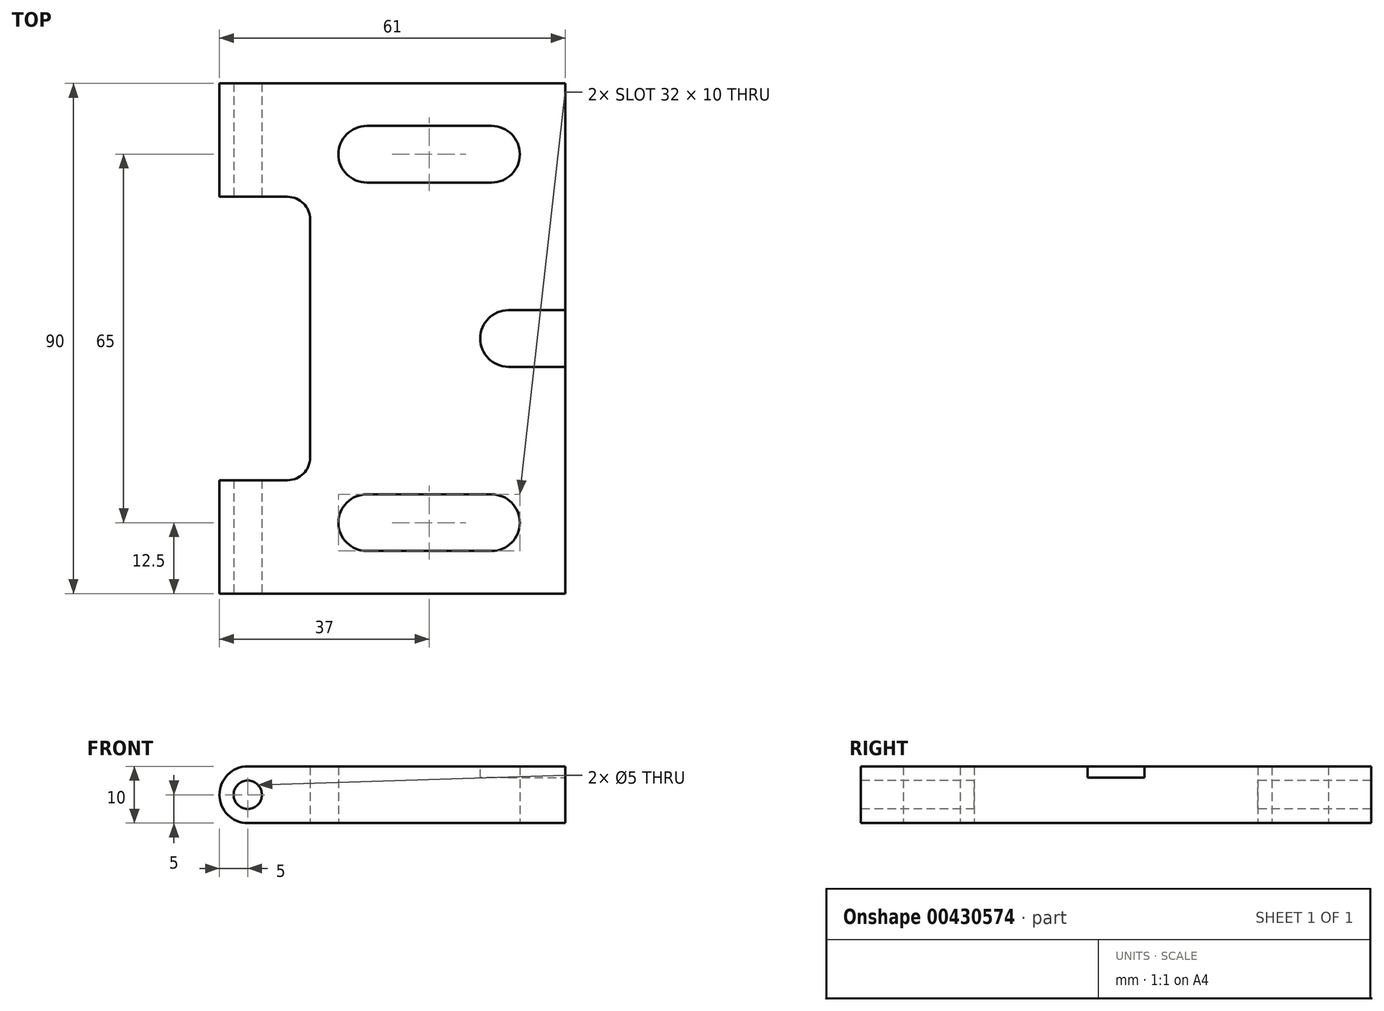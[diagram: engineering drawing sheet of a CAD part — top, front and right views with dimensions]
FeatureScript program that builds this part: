
annotation { "Feature Type Name" : "Feature", "Feature Type Description" : "" }
export const myFeature = defineFeature(function(context is Context, id is Id, definition is map)
    precondition{}
    {
        {
            var Q0;
            Q0=qCreatedBy(makeId("Top.planeOp"),FACE);
            var sketch = newSketch(context, id + "F0", { "sketchPlane" : qUnion([Q0])});
            skLineSegment(sketch, "E0.bottom", {"start": v(56, -45) * mm, "end": v(13, -45) * mm});
            skLineSegment(sketch, "E0.top", {"start": v(56, 45) * mm, "end": v(13, 45) * mm});
            skPoint(sketch, "E0.middle", {"position": v(0, 0) * mm});
            skLineSegment(sketch, "E1.bottom", {"start": v(11, -25) * mm, "end": v(-5, -25) * mm});
            skLineSegment(sketch, "E1.top", {"start": v(11, 25) * mm, "end": v(-5, 25) * mm});
            skPoint(sketch, "E1.middle", {"position": v(13, 0) * mm});
            skLineSegment(sketch, "E2", {"start": v(56, 45) * mm, "end": v(56, -45) * mm});
            skLineSegment(sketch, "E3", {"start": v(13, 45) * mm, "end": v(-5, 45) * mm});
            skLineSegment(sketch, "E4", {"start": v(-5, 45) * mm, "end": v(-5, 25) * mm});
            skLineSegment(sketch, "E5", {"start": v(13, -45) * mm, "end": v(-5, -45) * mm});
            skLineSegment(sketch, "E6", {"start": v(-5, -45) * mm, "end": v(-5, -25) * mm});
            skLineSegment(sketch, "E7", {"start": v(11, 25) * mm, "end": v(11, -25) * mm});
            skLineSegment(sketch, "E8", {"start": v(13, 45) * mm, "end": v(13, -45) * mm, "construction": true});
            skLineSegment(sketch, "E9.bottom", {"start": v(43, 27.5) * mm, "end": v(21, 27.5) * mm});
            skLineSegment(sketch, "E9.top", {"start": v(43, 37.5) * mm, "end": v(21, 37.5) * mm});
            skPoint(sketch, "E9.middle", {"position": v(21, 32.5) * mm});
            skArc(sketch, "E10", {"start": v(43, 37.5) * mm, "mid": v(48, 32.5) * mm, "end": v(43, 27.5) * mm});
            skArc(sketch, "E11", {"start": v(21, 37.5) * mm, "mid": v(16, 32.5) * mm, "end": v(21, 27.5) * mm});
            skLineSegment(sketch, "E12", {"start": v(21, 32.5) * mm, "end": v(43, 32.5) * mm, "construction": true});
            skLineSegment(sketch, "E13", {"start": v(0, 0) * mm, "end": v(37.1, 0) * mm, "construction": true});
            skArc(sketch, "E14.MirrorCS", {"start": v(43, -37.5) * mm, "mid": v(48, -32.5) * mm, "end": v(43, -27.5) * mm});
            skArc(sketch, "E15.MirrorCS", {"start": v(21, -37.5) * mm, "mid": v(16, -32.5) * mm, "end": v(21, -27.5) * mm});
            skLineSegment(sketch, "E16.MirrorCS", {"start": v(43, -37.5) * mm, "end": v(21, -37.5) * mm});
            skLineSegment(sketch, "E17.MirrorCS", {"start": v(43, -27.5) * mm, "end": v(21, -27.5) * mm});
            skSolve(sketch);
        }
        {
            var Q0;
            Q0=makeQuery(id+"F0.imprint","IMPRINT",FACE,{"disambiguationData":[TD([[makeQuery(id+"F0.imprint","IMPRINT",EDGE,{"derivedFrom":sQuery(id+"F0.wireOp",EDGE,"E0.bottom")}),-1.0]])]});
            extrude(context, id + "F1", {"entities" : qUnion([Q0]), "endBound" : BoundingType.SYMMETRIC, "depth" : 10 * mm, "offsetDistance" : 25 * mm});
        }
        {
            var Q0;
            Q0=makeQuery(id+"F1.opExtrude","SWEPT_FACE",FACE,{"disambiguationData":[OSD([sQuery(id+"F0.wireOp",EDGE,"E5")])]});
            var sketch = newSketch(context, id + "F2", { "sketchPlane" : qUnion([Q0])});
            skPoint(sketch, "E18", {"position": v(0, 0) * mm});
            skSolve(sketch);
        }
        {
            var Q0;
            Q0=sQuery(id+"F2.wireOp",VERTEX,"E18");
            var Q1;
            Q1=makeQuery(id+"F1.opExtrude","SWEPT_BODY",BODY,{"disambiguationData":[OSD([sQuery(id+"F0.wireOp",EDGE,"E0.bottom"),sQuery(id+"F0.wireOp",EDGE,"E0.top"),sQuery(id+"F0.wireOp",EDGE,"E0.left"),sQuery(id+"F0.wireOp",EDGE,"E0.right"),sQuery(id+"F0.wireOp",EDGE,"E1.bottom"),sQuery(id+"F0.wireOp",EDGE,"E1.top"),sQuery(id+"F0.wireOp",EDGE,"E1.left"),sQuery(id+"F0.wireOp",EDGE,"a411cbda-2916-457d-ac5a-dbeaaecaf6cb.trimOffspring")])]});
            hole(context, id + "F3", {"style" : HoleStyle.SIMPLE, "endStyle" : HoleEndStyle.THROUGH, "standardTappedOrClearance" : lookupTablePath({ "standard" : "ISO", "size" : "5", "type" : "Drilled" }), "standardBlindInLast" : lookupTablePath({ "standard" : "ISO", "size" : "5", "type" : "Drilled" }), "holeDiameter" : 5 * mm, "isTappedThrough" : true, "tappedDepth" : 12 * mm, "tapClearance" : 3, "locations" : qUnion([Q0]), "scope" : qUnion([Q1])});
        }
        {
            var Q0;
            Q0=makeQuery(id+"F1.opExtrude","CAP_EDGE",EDGE,{"disambiguationData":[OSD([sQuery(id+"F0.wireOp",EDGE,"E1.left")])],"isStart":false});
            var Q1;
            Q1=makeQuery(id+"F1.opExtrude","CAP_EDGE",EDGE,{"disambiguationData":[OSD([sQuery(id+"F0.wireOp",EDGE,"E1.left")])],"isStart":true});
            var Q2;
            Q2=makeQuery(id+"F1.opExtrude","CAP_EDGE",EDGE,{"disambiguationData":[OSD([sQuery(id+"F0.wireOp",EDGE,"E6")])],"isStart":false});
            var Q3;
            Q3=makeQuery(id+"F1.opExtrude","CAP_EDGE",EDGE,{"disambiguationData":[OSD([sQuery(id+"F0.wireOp",EDGE,"E6")])],"isStart":true});
            var Q4;
            Q4=makeQuery(id+"F1.opExtrude","CAP_EDGE",EDGE,{"disambiguationData":[OSD([sQuery(id+"F0.wireOp",EDGE,"E4")])],"isStart":false});
            var Q5;
            Q5=makeQuery(id+"F1.opExtrude","CAP_EDGE",EDGE,{"disambiguationData":[OSD([sQuery(id+"F0.wireOp",EDGE,"E4")])],"isStart":true});
            fillet(context, id + "F4", {"entities" : qUnion([Q0, Q1, Q2, Q3, Q4, Q5]), "radius" : 5 * mm, "tangentPropagation" : true, "allowEdgeOverflow" : false});
        }
        {
            var Q0;
            Q0=makeQuery(id+"F1.opExtrude","SWEPT_EDGE",EDGE,{"disambiguationData":[OSD([sQuery(id+"F0.wireOp",EDGE,"E1.top"),sQuery(id+"F0.wireOp",EDGE,"E7")])]});
            var Q1;
            Q1=makeQuery(id+"F1.opExtrude","SWEPT_EDGE",EDGE,{"disambiguationData":[OSD([sQuery(id+"F0.wireOp",EDGE,"E1.bottom"),sQuery(id+"F0.wireOp",EDGE,"E7")])]});
            fillet(context, id + "F5", {"entities" : qUnion([Q0, Q1]), "radius" : 4 * mm, "tangentPropagation" : true, "allowEdgeOverflow" : false});
        }
        {
            var Q0;
            Q0=makeQuery(id+"F1.opExtrude","CAP_FACE",FACE,{"disambiguationData":[OSD([sQuery(id+"F0.wireOp",EDGE,"E0.bottom"),sQuery(id+"F0.wireOp",EDGE,"E0.top"),sQuery(id+"F0.wireOp",EDGE,"E1.bottom"),sQuery(id+"F0.wireOp",EDGE,"E1.top"),sQuery(id+"F0.wireOp",EDGE,"E2"),sQuery(id+"F0.wireOp",EDGE,"E3"),sQuery(id+"F0.wireOp",EDGE,"E4"),sQuery(id+"F0.wireOp",EDGE,"E5"),sQuery(id+"F0.wireOp",EDGE,"E6"),sQuery(id+"F0.wireOp",EDGE,"E7"),sQuery(id+"F0.wireOp",EDGE,"E9.bottom"),sQuery(id+"F0.wireOp",EDGE,"E9.top"),sQuery(id+"F0.wireOp",EDGE,"E10"),sQuery(id+"F0.wireOp",EDGE,"E11"),sQuery(id+"F0.wireOp",EDGE,"E14.MirrorCS"),sQuery(id+"F0.wireOp",EDGE,"E15.MirrorCS"),sQuery(id+"F0.wireOp",EDGE,"E16.MirrorCS"),sQuery(id+"F0.wireOp",EDGE,"E17.MirrorCS")])],"isStart":false});
            var sketch = newSketch(context, id + "F6", { "sketchPlane" : qUnion([Q0])});
            skLineSegment(sketch, "E19.bottom", {"start": v(46, -5) * mm, "end": v(56, -5) * mm});
            skLineSegment(sketch, "E19.top", {"start": v(46, 5) * mm, "end": v(56, 5) * mm});
            skLineSegment(sketch, "E19.right", {"start": v(56, -5) * mm, "end": v(56, 5) * mm});
            skPoint(sketch, "E19.middle.positionSnap0", {"position": v(11, 0) * mm});
            skPoint(sketch, "E19.centerSnap0", {"position": v(11, 0) * mm});
            skArc(sketch, "E20", {"start": v(46, 5) * mm, "mid": v(41, 0) * mm, "end": v(46, -5) * mm});
            skSolve(sketch);
        }
        {
            var Q0;
            Q0 = qSketchRegion(id + "F6", true);
            extrude(context, id + "F7", {"entities" : qUnion([Q0]), "operationType" : NewBodyOperationType.REMOVE, "oppositeDirection" : true, "depth" : 2 * mm, "offsetDistance" : 25 * mm});
        }
    });
